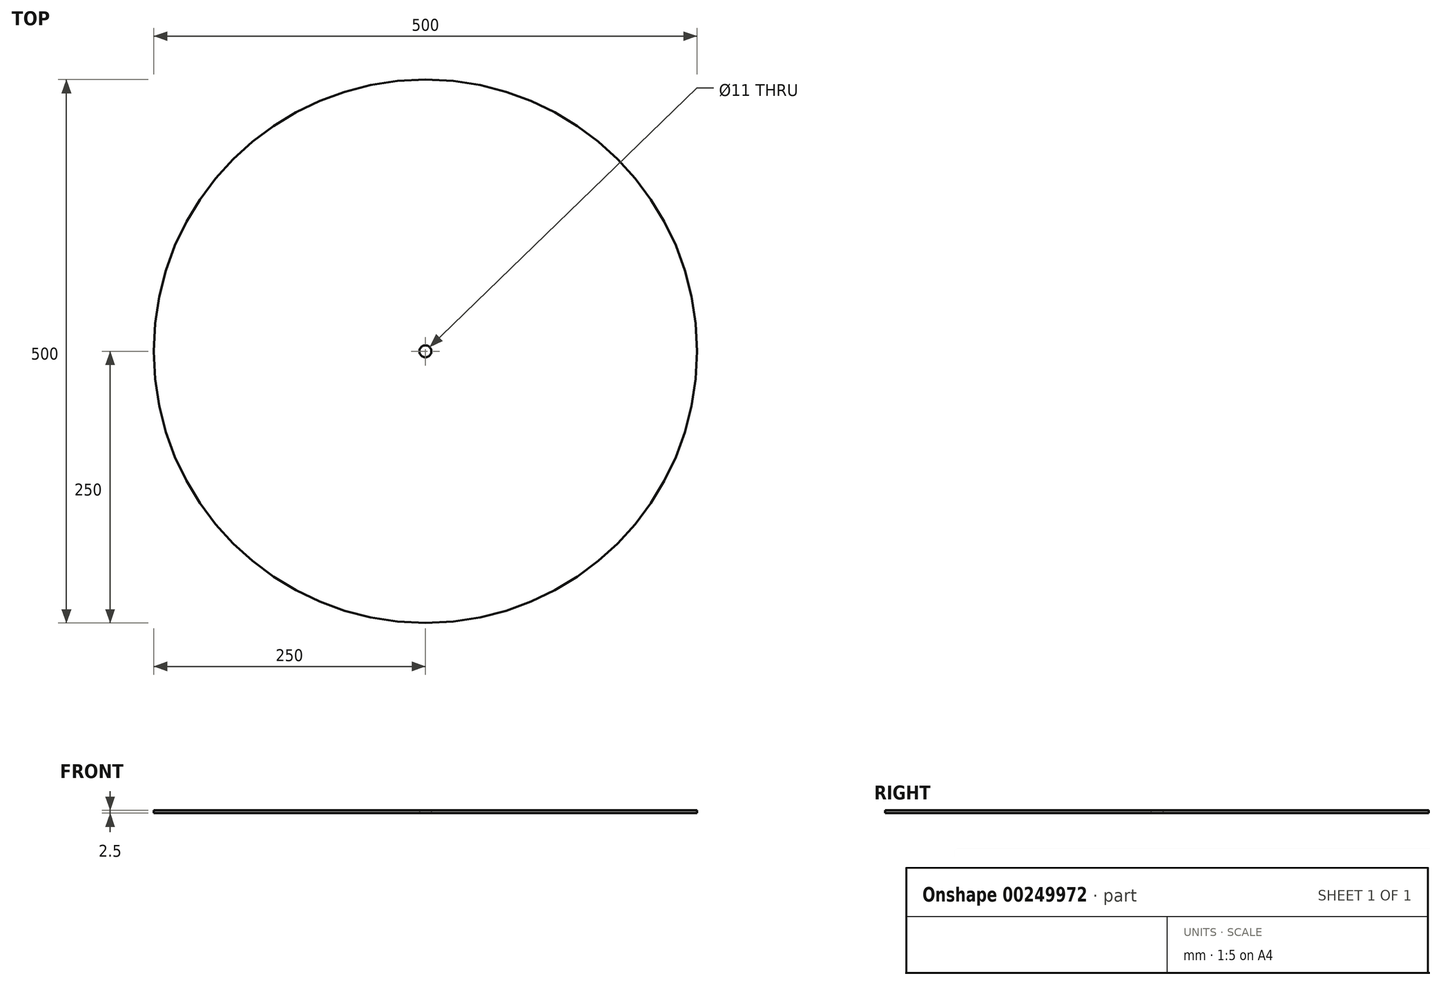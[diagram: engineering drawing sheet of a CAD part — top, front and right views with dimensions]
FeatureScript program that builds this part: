
annotation { "Feature Type Name" : "Feature", "Feature Type Description" : "" }
export const myFeature = defineFeature(function(context is Context, id is Id, definition is map)
    precondition{}
    {
        {
            var Q0;
            Q0=qCreatedBy(makeId("Top.planeOp"),FACE);
            var sketch = newSketch(context, id + "F0", { "sketchPlane" : qUnion([Q0])});
            skCircle(sketch, "E0", {"center": v(0, 0) * mm, "radius": 250 * mm});
            skCircle(sketch, "E1", {"center": v(0, 0) * mm, "radius": 5.5 * mm});
            skSolve(sketch);
        }
        {
            var Q0;
            Q0=makeQuery(id+"F0.imprint","IMPRINT",FACE,{"disambiguationData":[TD([[makeQuery(id+"F0.imprint","IMPRINT",EDGE,{"derivedFrom":sQuery(id+"F0.wireOp",EDGE,"E0")}),1.0]])]});
            extrude(context, id + "F1", {"entities" : qUnion([Q0]), "depth" : 2.5 * mm});
        }
    });
